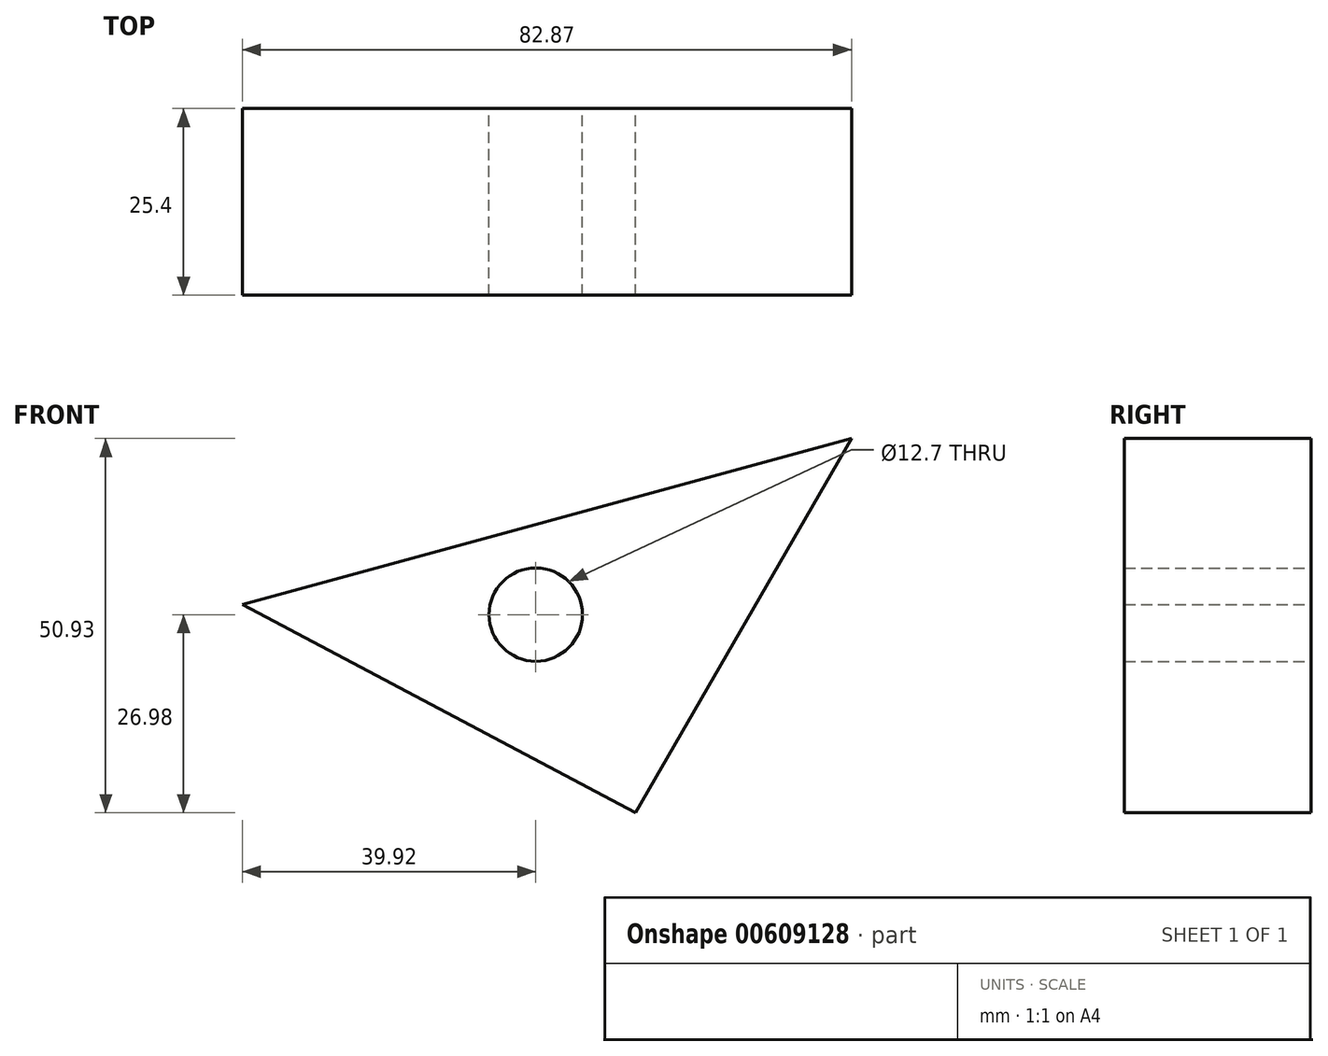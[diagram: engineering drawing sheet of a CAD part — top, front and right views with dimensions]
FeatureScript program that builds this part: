
annotation { "Feature Type Name" : "Feature", "Feature Type Description" : "" }
export const myFeature = defineFeature(function(context is Context, id is Id, definition is map)
    precondition{}
    {
        {
            var Q0;
            Q0=qCreatedBy(makeId("Front.planeOp"),FACE);
            var sketch = newSketch(context, id + "F0", { "sketchPlane" : qUnion([Q0])});
            skLineSegment(sketch, "E0", {"start": v(0, 0) * mm, "end": v(-53.47, 28.37) * mm});
            skLineSegment(sketch, "E1", {"start": v(-53.47, 28.37) * mm, "end": v(29.4, 50.93) * mm});
            skLineSegment(sketch, "E2", {"start": v(29.4, 50.93) * mm, "end": v(0, 0) * mm});
            skSolve(sketch);
        }
        {
            var Q0;
            Q0 = qSketchRegion(id + "F0", true);
            extrude(context, id + "F1", {"entities" : qUnion([Q0]), "depth" : 25.4 * mm, "offsetDistance" : 25.4 * mm});
        }
        {
            var Q0;
            Q0=makeQuery(id+"F1.opExtrude","CAP_FACE",FACE,{"disambiguationData":[OSD([sQuery(id+"F0.wireOp",EDGE,"E0"),sQuery(id+"F0.wireOp",EDGE,"E1"),sQuery(id+"F0.wireOp",EDGE,"E2")])],"isStart":true});
            var sketch = newSketch(context, id + "F2", { "sketchPlane" : qUnion([Q0])});
            skCircle(sketch, "E3", {"center": v(13.55, 26.98) * mm, "radius": 6.35 * mm});
            skSolve(sketch);
        }
        {
            var Q0;
            Q0=sQuery(id+"F2.wireOp",VERTEX,"E3.center");
            var Q1;
            Q1=makeQuery(id+"F1.opExtrude","SWEPT_BODY",BODY,{"disambiguationData":[OSD([sQuery(id+"F0.wireOp",EDGE,"E0"),sQuery(id+"F0.wireOp",EDGE,"E1"),sQuery(id+"F0.wireOp",EDGE,"E2")])]});
            hole(context, id + "F3", {"style" : HoleStyle.SIMPLE, "endStyle" : HoleEndStyle.THROUGH, "holeDiameter" : 12.7 * mm, "majorDiameter" : 6.35 * mm, "isTappedThrough" : true, "tappedDepth" : 12.7 * mm, "tapClearance" : 3, "startFromSketch" : true, "locations" : qUnion([Q0]), "scope" : qUnion([Q1])});
        }
    });
